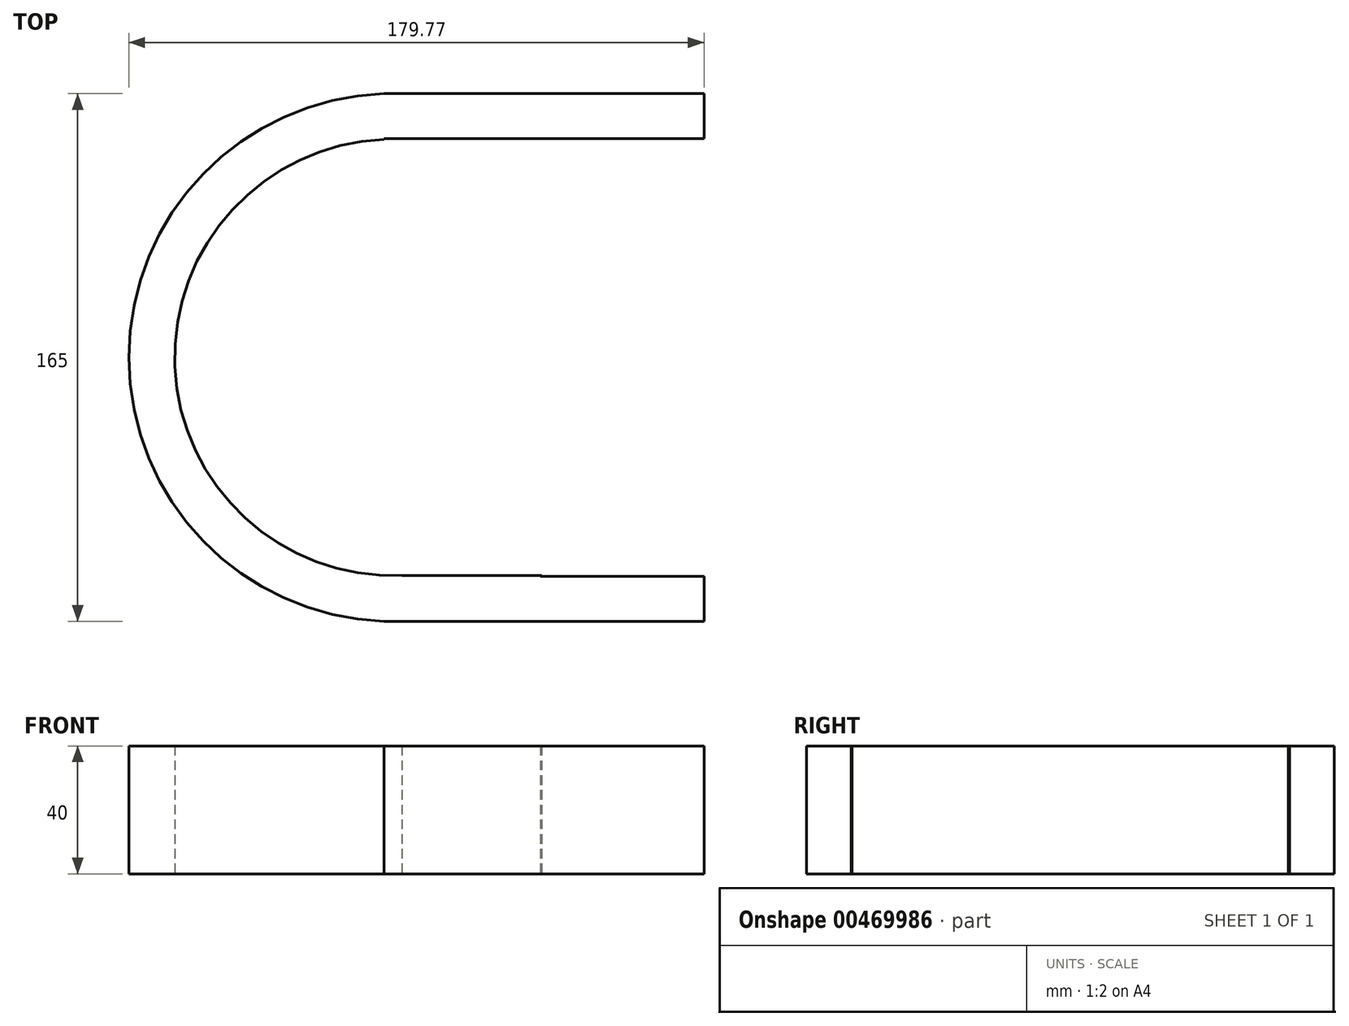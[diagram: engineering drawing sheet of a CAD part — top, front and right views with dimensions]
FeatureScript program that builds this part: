
annotation { "Feature Type Name" : "Feature", "Feature Type Description" : "" }
export const myFeature = defineFeature(function(context is Context, id is Id, definition is map)
    precondition{}
    {
        {
            var Q0;
            Q0=qCreatedBy(makeId("Top.planeOp"),FACE);
            var sketch = newSketch(context, id + "F0", { "sketchPlane" : qUnion([Q0])});
            skCircle(sketch, "E0", {"center": v(2.78, 0) * mm, "radius": 82.55 * mm});
            skLineSegment(sketch, "E1.bottom", {"start": v(0, 82.5) * mm, "end": v(100, 82.5) * mm});
            skLineSegment(sketch, "E1.top", {"start": v(0, 68.5) * mm, "end": v(100, 68.5) * mm});
            skLineSegment(sketch, "E1.left", {"start": v(0, 82.5) * mm, "end": v(0, 68.5) * mm});
            skLineSegment(sketch, "E1.right", {"start": v(100, 82.5) * mm, "end": v(100, 68.5) * mm});
            skLineSegment(sketch, "E2.bottom", {"start": v(0, -82.5) * mm, "end": v(100, -82.5) * mm});
            skLineSegment(sketch, "E2.top", {"start": v(0, -68.5) * mm, "end": v(100, -68.5) * mm});
            skLineSegment(sketch, "E2.left", {"start": v(0, -82.5) * mm, "end": v(0, -68.5) * mm});
            skLineSegment(sketch, "E2.right", {"start": v(100, -82.5) * mm, "end": v(100, -68.5) * mm});
            skCircle(sketch, "E3.0", {"center": v(2.78, 0) * mm, "radius": 68.25 * mm});
            skSolve(sketch);
        }
        {
            var Q0;
            {var subQ5=sQuery(id+"F0.wireOp",EDGE,"E1.left");Q0=makeQuery(id+"F0.imprint","IMPRINT",FACE,{"disambiguationData":[TD([[makeQuery(id+"F0.imprint","IMPRINT",EDGE,{"derivedFrom":subQ5}),1.0]])]});}
            var Q1;
            {var subQ5=sQuery(id+"F0.wireOp",EDGE,"E1.right");Q1=makeQuery(id+"F0.imprint","IMPRINT",FACE,{"disambiguationData":[TD([[makeQuery(id+"F0.imprint","IMPRINT",EDGE,{"derivedFrom":subQ5}),-1.0]])]});}
            var Q2;
            {var subQ5=sQuery(id+"F0.wireOp",EDGE,"E2.right");Q2=makeQuery(id+"F0.imprint","IMPRINT",FACE,{"disambiguationData":[TD([[makeQuery(id+"F0.imprint","IMPRINT",EDGE,{"derivedFrom":subQ5}),1.0]])]});}
            var Q3;
            {var subQ5=sQuery(id+"F0.wireOp",EDGE,"E2.left");Q3=makeQuery(id+"F0.imprint","IMPRINT",FACE,{"disambiguationData":[TD([[makeQuery(id+"F0.imprint","IMPRINT",EDGE,{"derivedFrom":subQ5}),-1.0]])]});}
            var Q4;
            {var subQ0=sQuery(id+"F0.wireOp",EDGE,"E1.left");Q4=makeQuery(id+"F0.imprint","IMPRINT",FACE,{"disambiguationData":[TD([[makeQuery(id+"F0.imprint","IMPRINT",EDGE,{"derivedFrom":subQ0}),-1.0]])]});}
            extrude(context, id + "F1", {"entities" : qUnion([Q0, Q1, Q2, Q3, Q4]), "depth" : 40 * mm, "offsetDistance" : 25 * mm});
        }
        {
            var Q0;
            Q0=makeQuery(id+"F1.opExtrude","CAP_FACE",FACE,{"disambiguationData":[OSD([sQuery(id+"F0.wireOp",EDGE,"E0"),sQuery(id+"F0.wireOp",EDGE,"E1.bottom"),sQuery(id+"F0.wireOp",EDGE,"E1.top"),sQuery(id+"F0.wireOp",EDGE,"E1.right"),sQuery(id+"F0.wireOp",EDGE,"E2.bottom"),sQuery(id+"F0.wireOp",EDGE,"E2.top"),sQuery(id+"F0.wireOp",EDGE,"E2.right"),sQuery(id+"F0.wireOp",EDGE,"E3.0")])],"isStart":false});
            var sketch = newSketch(context, id + "F2", { "sketchPlane" : qUnion([Q0])});
            skLineSegment(sketch, "E4.bottom", {"start": v(128.25, 68.5) * mm, "end": v(0, 68.5) * mm});
            skLineSegment(sketch, "E4.top", {"start": v(128.25, -68.2) * mm, "end": v(0, -68.2) * mm});
            skLineSegment(sketch, "E4.left", {"start": v(128.25, 68.5) * mm, "end": v(128.25, -68.2) * mm});
            skLineSegment(sketch, "E4.right", {"start": v(0, 68.5) * mm, "end": v(0, -68.2) * mm});
            skSolve(sketch);
        }
        {
            var Q0;
            {var subQ0=sQuery(id+"F2.wireOp",EDGE,"E4.left");Q0=makeQuery(id+"F2.imprint","IMPRINT",FACE,{"disambiguationData":[TD([[makeQuery(id+"F2.imprint","IMPRINT",EDGE,{"derivedFrom":subQ0}),-1.0]])]});}
            var Q1;
            {var subQ1=sQuery(id+"F2.wireOp",EDGE,"E4.top");var subQ2=makeQuery(id+"F1.opExtrude","CAP_EDGE",EDGE,{"disambiguationData":[OSD([sQuery(id+"F0.wireOp",EDGE,"E3.0")])],"isStart":false});var subQ4=makeQuery(id+"F2.imprint","INTERSECT",VERTEX,{"derivedFrom":[subQ2,subQ1]});Q1=makeQuery(id+"F2.imprint","IMPRINT",FACE,{"disambiguationData":[TD([[makeQuery(id+"F2.imprint","IMPRINT",EDGE,{"disambiguationData":[TD([[subQ4,-1.0]])],"derivedFrom":subQ2}),1.0]])]});}
            var Q2;
            {var subQ0=sQuery(id+"F2.wireOp",EDGE,"E4.bottom");var subQ8=sQuery(id+"F2.wireOp",EDGE,"E4.right");var subQ9=makeQuery(id+"F2.imprint","INTERSECT",VERTEX,{"derivedFrom":[subQ0,subQ8]});Q2=makeQuery(id+"F2.imprint","IMPRINT",FACE,{"disambiguationData":[TD([[makeQuery(id+"F2.imprint","IMPRINT",EDGE,{"disambiguationData":[TD([[subQ9,-1.0]])],"derivedFrom":subQ8}),1.0]])]});}
            extrude(context, id + "F3", {"entities" : qUnion([Q0, Q1, Q2]), "operationType" : NewBodyOperationType.REMOVE, "oppositeDirection" : true, "depth" : 43.6 * mm, "offsetDistance" : 25 * mm});
        }
    });
